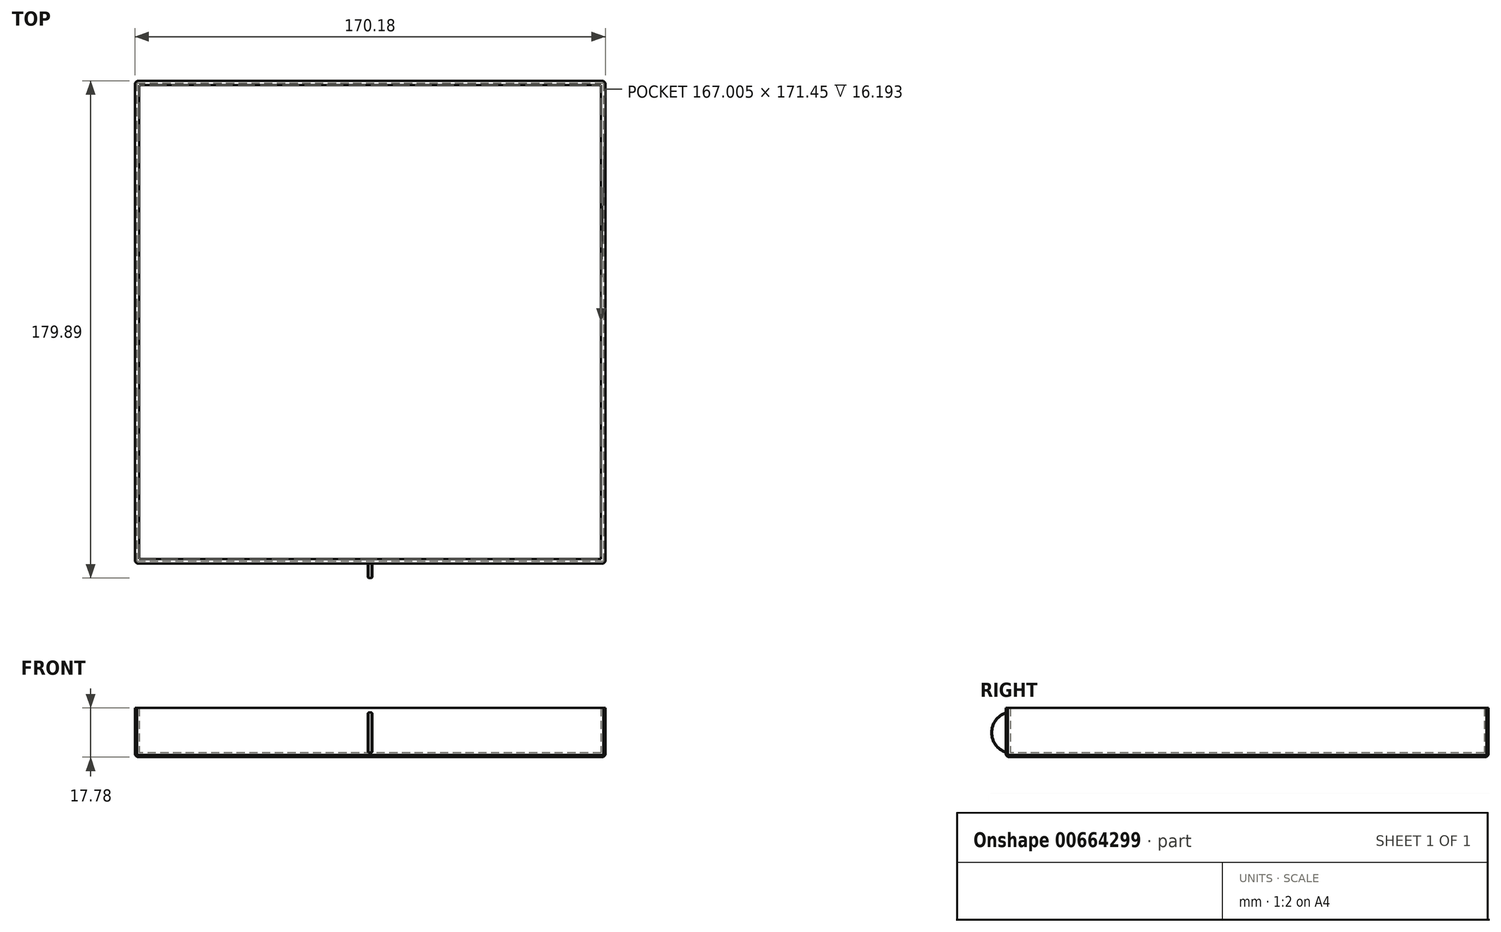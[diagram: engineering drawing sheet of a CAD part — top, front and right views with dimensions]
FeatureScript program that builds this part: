
annotation { "Feature Type Name" : "Feature", "Feature Type Description" : "" }
export const myFeature = defineFeature(function(context is Context, id is Id, definition is map)
    precondition{}
    {
        {
            var Q0;
            Q0=qCreatedBy(makeId("Top.planeOp"),FACE);
            var sketch = newSketch(context, id + "F0", { "sketchPlane" : qUnion([Q0])});
            skLineSegment(sketch, "E0.bottom", {"start": v(-85.1, 87.31) * mm, "end": v(85.1, 87.31) * mm});
            skLineSegment(sketch, "E0.top", {"start": v(-85.1, -87.31) * mm, "end": v(85.1, -87.31) * mm});
            skLineSegment(sketch, "E0.left", {"start": v(-85.1, 87.31) * mm, "end": v(-85.1, -87.31) * mm});
            skLineSegment(sketch, "E0.right", {"start": v(85.1, 87.31) * mm, "end": v(85.1, -87.31) * mm});
            skSolve(sketch);
        }
        {
            var Q0;
            Q0=qSketchRegion(id+"F0",true);
            extrude(context, id + "F1", {"entities" : qUnion([Q0]), "depth" : 1.59 * mm, "offsetDistance" : 25.4 * mm});
        }
        {
            var Q0;
            Q0=makeQuery(id+"F1.opExtrude","CAP_FACE",FACE,{"disambiguationData":[OSD([sQuery(id+"F0.wireOp",EDGE,"E0.bottom"),sQuery(id+"F0.wireOp",EDGE,"E0.top"),sQuery(id+"F0.wireOp",EDGE,"E0.left"),sQuery(id+"F0.wireOp",EDGE,"E0.right")])],"isStart":false});
            var sketch = newSketch(context, id + "F2", { "sketchPlane" : qUnion([Q0])});
            skLineSegment(sketch, "E1.0", {"start": v(-83.5, 85.73) * mm, "end": v(-83.5, -85.73) * mm});
            skLineSegment(sketch, "E1.1", {"start": v(83.5, 85.73) * mm, "end": v(-83.5, 85.73) * mm});
            skLineSegment(sketch, "E1.2", {"start": v(83.5, -85.73) * mm, "end": v(83.5, 85.73) * mm});
            skLineSegment(sketch, "E1.3", {"start": v(-83.5, -85.73) * mm, "end": v(83.5, -85.73) * mm});
            skLineSegment(sketch, "E2.0", {"start": v(-85.1, 87.31) * mm, "end": v(-85.1, -87.31) * mm});
            skLineSegment(sketch, "E2.1", {"start": v(-85.1, -87.31) * mm, "end": v(85.1, -87.31) * mm});
            skLineSegment(sketch, "E2.2", {"start": v(85.1, 87.31) * mm, "end": v(85.1, -87.31) * mm});
            skLineSegment(sketch, "E2.3", {"start": v(-85.1, 87.31) * mm, "end": v(85.1, 87.31) * mm});
            skSolve(sketch);
        }
        {
            var Q0;
            Q0=qSketchRegion(id+"F2",true);
            extrude(context, id + "F3", {"entities" : qUnion([Q0]), "operationType" : NewBodyOperationType.ADD, "depth" : 16.2 * mm, "offsetDistance" : 25.4 * mm});
        }
        {
            var Q0;
            Q0=qCreatedBy(makeId("Right.planeOp"),FACE);
            var sketch = newSketch(context, id + "F4", { "sketchPlane" : qUnion([Q0])});
            skArc(sketch, "E3", {"start": v(-87.31, 16.14) * mm, "mid": v(-92.58, 8.9) * mm, "end": v(-87.31, 1.64) * mm});
            skLineSegment(sketch, "E4", {"start": v(-87.31, 16.14) * mm, "end": v(-87.31, 1.64) * mm});
            skSolve(sketch);
        }
        {
            var Q0;
            Q0=qSketchRegion(id+"F4",true);
            extrude(context, id + "F5", {"entities" : qUnion([Q0]), "operationType" : NewBodyOperationType.ADD, "endBound" : BoundingType.SYMMETRIC, "depth" : 1.59 * mm, "offsetDistance" : 25.4 * mm});
        }
        {
            var Q0;
            Q0=makeQuery(id+"F1.opExtrude","CAP_EDGE",EDGE,{"disambiguationData":[OSD([sQuery(id+"F0.wireOp",EDGE,"E0.top")])],"isStart":true});
            var Q1;
            Q1=makeQuery(id+"F1.opExtrude","CAP_EDGE",EDGE,{"disambiguationData":[OSD([sQuery(id+"F0.wireOp",EDGE,"E0.right")])],"isStart":true});
            var Q2;
            Q2=makeQuery(id+"F1.opExtrude","CAP_EDGE",EDGE,{"disambiguationData":[OSD([sQuery(id+"F0.wireOp",EDGE,"E0.left")])],"isStart":true});
            var Q3;
            Q3=makeQuery(id+"F1.opExtrude","CAP_EDGE",EDGE,{"disambiguationData":[OSD([sQuery(id+"F0.wireOp",EDGE,"E0.bottom")])],"isStart":true});
            var Q4;
            Q4=makeQuery(id+"F3.boolean.opBoolean","MERGE",EDGE,{"derivedFrom":[makeQuery(id+"F1.opExtrude","SWEPT_EDGE",EDGE,{"disambiguationData":[OSD([sQuery(id+"F0.wireOp",EDGE,"E0.top"),sQuery(id+"F0.wireOp",EDGE,"E0.left")])]}),makeQuery(id+"F3.opExtrude","SWEPT_EDGE",EDGE,{"disambiguationData":[OSD([sQuery(id+"F2.wireOp",EDGE,"E2.0"),sQuery(id+"F2.wireOp",EDGE,"E2.1")])]})]});
            var Q5;
            Q5=makeQuery(id+"F3.boolean.opBoolean","MERGE",EDGE,{"derivedFrom":[makeQuery(id+"F1.opExtrude","SWEPT_EDGE",EDGE,{"disambiguationData":[OSD([sQuery(id+"F0.wireOp",EDGE,"E0.top"),sQuery(id+"F0.wireOp",EDGE,"E0.right")])]}),makeQuery(id+"F3.opExtrude","SWEPT_EDGE",EDGE,{"disambiguationData":[OSD([sQuery(id+"F2.wireOp",EDGE,"E2.1"),sQuery(id+"F2.wireOp",EDGE,"E2.2")])]})]});
            var Q6;
            Q6=makeQuery(id+"F3.boolean.opBoolean","MERGE",EDGE,{"derivedFrom":[makeQuery(id+"F1.opExtrude","SWEPT_EDGE",EDGE,{"disambiguationData":[OSD([sQuery(id+"F0.wireOp",EDGE,"E0.bottom"),sQuery(id+"F0.wireOp",EDGE,"E0.right")])]}),makeQuery(id+"F3.opExtrude","SWEPT_EDGE",EDGE,{"disambiguationData":[OSD([sQuery(id+"F2.wireOp",EDGE,"E2.2"),sQuery(id+"F2.wireOp",EDGE,"E2.3")])]})]});
            var Q7;
            Q7=makeQuery(id+"F3.boolean.opBoolean","MERGE",EDGE,{"derivedFrom":[makeQuery(id+"F1.opExtrude","SWEPT_EDGE",EDGE,{"disambiguationData":[OSD([sQuery(id+"F0.wireOp",EDGE,"E0.bottom"),sQuery(id+"F0.wireOp",EDGE,"E0.left")])]}),makeQuery(id+"F3.opExtrude","SWEPT_EDGE",EDGE,{"disambiguationData":[OSD([sQuery(id+"F2.wireOp",EDGE,"E2.0"),sQuery(id+"F2.wireOp",EDGE,"E2.3")])]})]});
            chamfer(context, id + "F6", {"entities" : qUnion([Q0, Q1, Q2, Q3, Q4, Q5, Q6, Q7]), "width" : 0.76 * mm, "tangentPropagation" : true});
        }
        {
            var Q0;
            Q0=makeQuery(id+"F5.opExtrude","CAP_EDGE",EDGE,{"disambiguationData":[OSD([sQuery(id+"F4.wireOp",EDGE,"E4")])],"isStart":false});
            var Q1;
            Q1=makeQuery(id+"F5.opExtrude","CAP_EDGE",EDGE,{"disambiguationData":[OSD([sQuery(id+"F4.wireOp",EDGE,"E4")])],"isStart":true});
            var Q2;
            Q2=makeQuery(id+"F5.opExtrude","CAP_EDGE",EDGE,{"disambiguationData":[OSD([sQuery(id+"F4.wireOp",EDGE,"E3")])],"isStart":true});
            var Q3;
            Q3=makeQuery(id+"F5.opExtrude","CAP_EDGE",EDGE,{"disambiguationData":[OSD([sQuery(id+"F4.wireOp",EDGE,"E3")])],"isStart":false});
            chamfer(context, id + "F7", {"entities" : qUnion([Q0, Q1, Q2, Q3]), "width" : 0.25 * mm, "tangentPropagation" : true});
        }
    });
